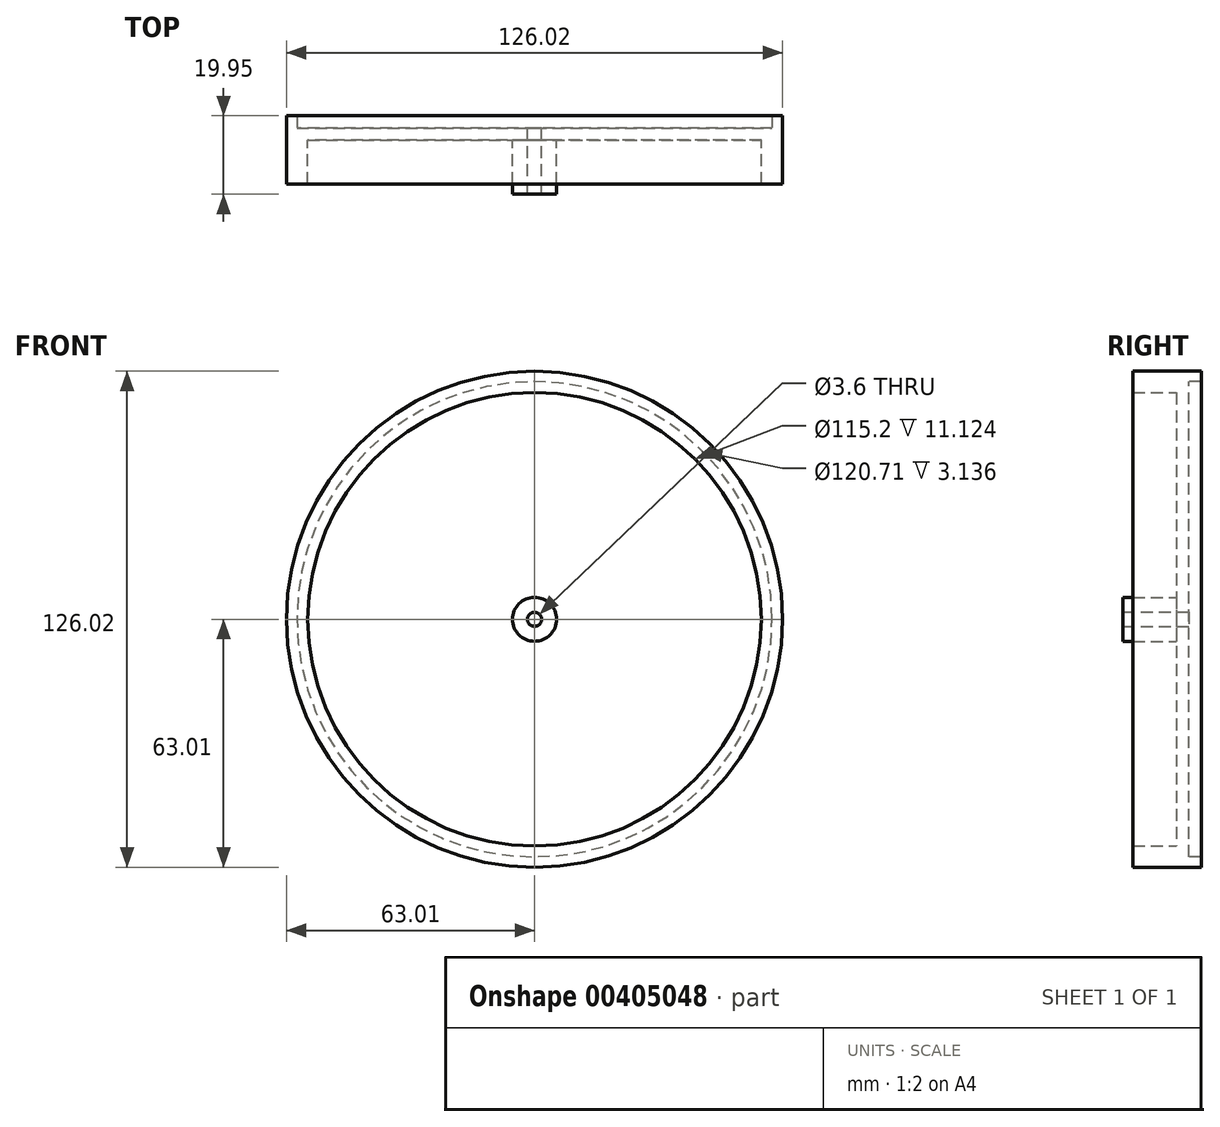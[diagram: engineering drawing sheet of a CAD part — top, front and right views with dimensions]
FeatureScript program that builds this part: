
annotation { "Feature Type Name" : "Feature", "Feature Type Description" : "" }
export const myFeature = defineFeature(function(context is Context, id is Id, definition is map)
    precondition{}
    {
        {
            var Q0;
            Q0=qCreatedBy(makeId("Right.planeOp"),FACE);
            var sketch = newSketch(context, id + "F0", { "sketchPlane" : qUnion([Q0])});
            skLineSegment(sketch, "E0", {"start": v(0, 63.01) * mm, "end": v(-17.4, 63.01) * mm});
            skLineSegment(sketch, "E1", {"start": v(-17.4, 63.01) * mm, "end": v(-17.4, 57.6) * mm});
            skLineSegment(sketch, "E2", {"start": v(-17.4, 57.6) * mm, "end": v(-6.27, 57.6) * mm});
            skLineSegment(sketch, "E3", {"start": v(-6.27, 57.6) * mm, "end": v(-6.27, 40.16) * mm});
            skLineSegment(sketch, "E4", {"start": v(-6.27, 40.16) * mm, "end": v(-6.27, 5.59) * mm});
            skLineSegment(sketch, "E5", {"start": v(-6.27, 5.59) * mm, "end": v(-19.95, 5.59) * mm});
            skLineSegment(sketch, "E6", {"start": v(-19.95, 5.59) * mm, "end": v(-19.95, 1.8) * mm});
            skLineSegment(sketch, "E7", {"start": v(-19.95, 1.8) * mm, "end": v(0, 1.8) * mm});
            skLineSegment(sketch, "E8", {"start": v(0, 1.8) * mm, "end": v(0, 63.01) * mm});
            skSolve(sketch);
        }
        {
            var Q0;
            Q0=qCreatedBy(makeId("Right.planeOp"),FACE);
            var sketch = newSketch(context, id + "F1", { "sketchPlane" : qUnion([Q0])});
            skLineSegment(sketch, "E9", {"start": v(0, 0) * mm, "end": v(-12.62, 0) * mm});
            skSolve(sketch);
        }
        {
            var Q0;
            Q0=makeQuery(id+"F0.imprint","IMPRINT",FACE,{"disambiguationData":[TD([[makeQuery(id+"F0.imprint","IMPRINT",EDGE,{"derivedFrom":sQuery(id+"F0.wireOp",EDGE,"E0")}),1.0]])]});
            var Q1;
            Q1=sQuery(id+"F1.wireOp",EDGE,"E9");
            revolve(context, id + "F2", {"entities" : qUnion([Q0]), "axis" : qUnion([Q1]), "revolveType" : RevolveType.FULL});
        }
        {
            var Q0;
            Q0=qCreatedBy(makeId("Right.planeOp"),FACE);
            var sketch = newSketch(context, id + "F3", { "sketchPlane" : qUnion([Q0])});
            skLineSegment(sketch, "E10", {"start": v(0, 64.3) * mm, "end": v(0, 0) * mm});
            skLineSegment(sketch, "E11.bottom", {"start": v(0, 60.35) * mm, "end": v(-3.14, 60.35) * mm});
            skLineSegment(sketch, "E11.top", {"start": v(0, 0) * mm, "end": v(-3.14, 0) * mm});
            skLineSegment(sketch, "E11.left", {"start": v(0, 60.35) * mm, "end": v(0, 0) * mm});
            skLineSegment(sketch, "E11.right", {"start": v(-3.14, 60.35) * mm, "end": v(-3.14, 0) * mm});
            skSolve(sketch);
        }
        {
            var Q0;
            Q0 = qSketchRegion(id + "F3", true);
            var Q1;
            Q1=sQuery(id+"F1.wireOp",EDGE,"E9");
            revolve(context, id + "F4", {"operationType" : NewBodyOperationType.REMOVE, "entities" : qUnion([Q0]), "axis" : qUnion([Q1]), "revolveType" : RevolveType.FULL, "oppositeDirection" : true});
        }
    });
